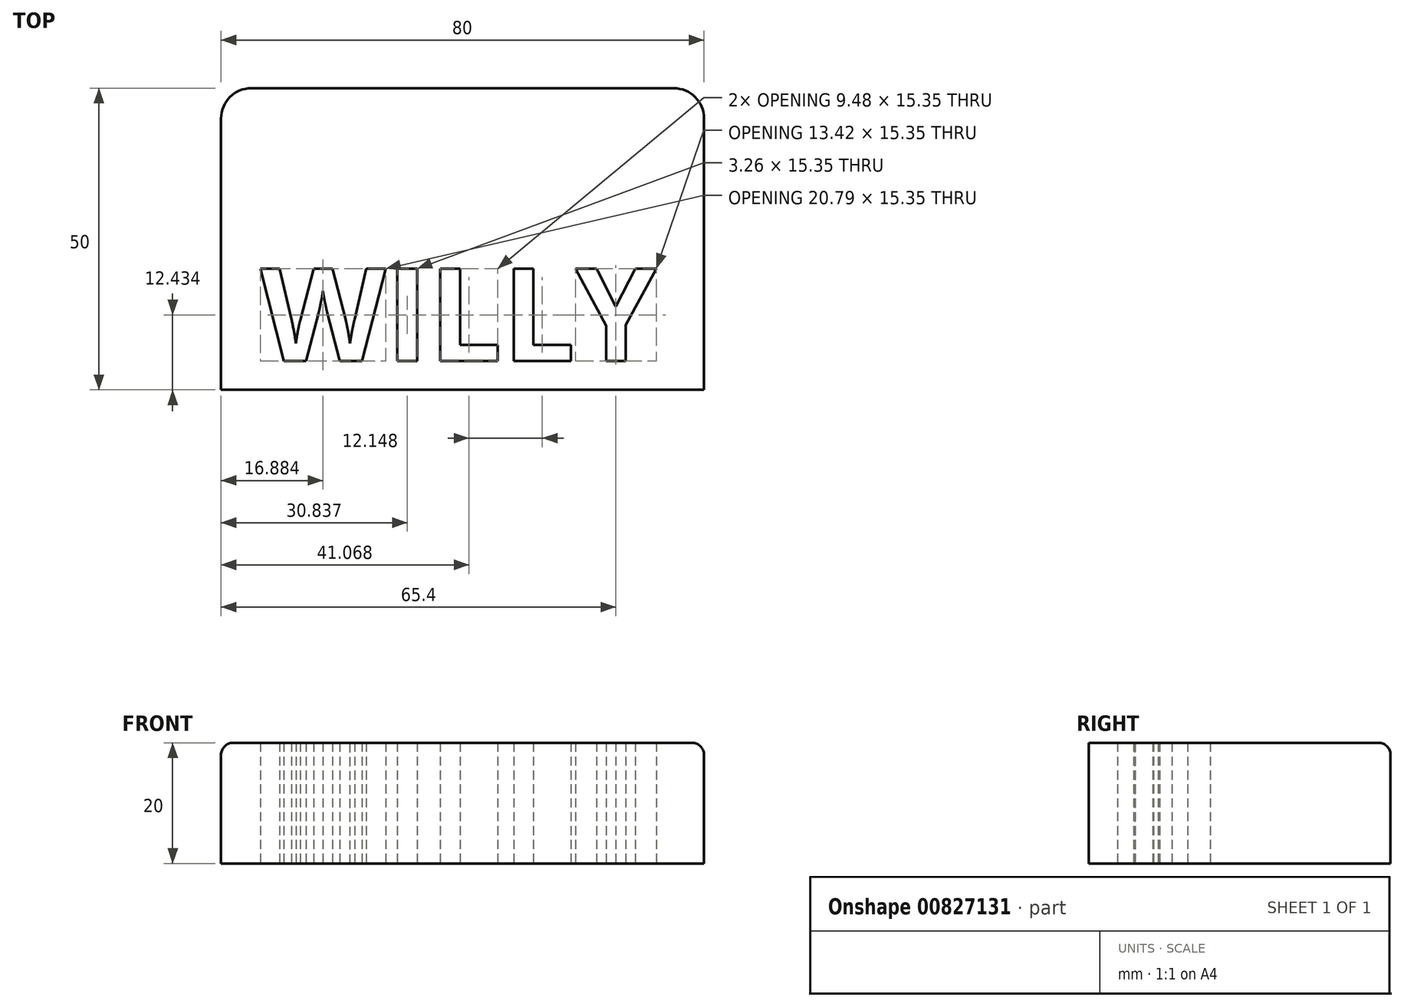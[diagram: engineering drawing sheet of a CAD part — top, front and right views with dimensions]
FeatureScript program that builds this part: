
annotation { "Feature Type Name" : "Feature", "Feature Type Description" : "" }
export const myFeature = defineFeature(function(context is Context, id is Id, definition is map)
    precondition{}
    {
        {
            var Q0;
            Q0=qCreatedBy(makeId("Top.planeOp"),FACE);
            var sketch = newSketch(context, id + "F0", { "sketchPlane" : qUnion([Q0])});
            skLineSegment(sketch, "E0.top", {"start": v(40, -25) * mm, "end": v(-40, -25) * mm});
            skLineSegment(sketch, "E0.left", {"start": v(40, 20) * mm, "end": v(40, -25) * mm});
            skLineSegment(sketch, "E0.right", {"start": v(-40, 20) * mm, "end": v(-40, -25) * mm});
            skPoint(sketch, "E0.middle", {"position": v(0, 0) * mm});
            skArc(sketch, "E1.filletArc", {"start": v(-35, 25) * mm, "mid": v(-38.54, 23.54) * mm, "end": v(-40, 20) * mm});
            skArc(sketch, "E2.filletArc", {"start": v(40, 20) * mm, "mid": v(38.54, 23.54) * mm, "end": v(35, 25) * mm});
            skPoint(sketch, "E3.middle", {"position": v(0, -12.5) * mm});
            skText(sketch, "E4", { "text": "WILLY", "fontName": "OpenSans-Bold.ttf"});
            skLineSegment(sketch, "E5", {"start": v(-35, 25) * mm, "end": v(35, 25) * mm});
            const initialGuessF0  = {"E4": [-0.03351, -0.02024, 1, 0, 0.01548]};
            skSetInitialGuess(sketch, initialGuessF0);
            skSolve(sketch);
        }
        {
            var Q0;
            Q0=makeQuery(id+"F0.imprint","IMPRINT",FACE,{"disambiguationData":[TD([[makeQuery(id+"F0.imprint","IMPRINT",EDGE,{"derivedFrom":sQuery(id+"F0.wireOp",EDGE,"E0.top")}),-1.0]])]});
            extrude(context, id + "F1", {"entities" : qUnion([Q0]), "depth" : 20 * mm, "offsetDistance" : 25 * mm});
        }
        {
            var Q0;
            Q0=makeQuery(id+"F1.opExtrude","CAP_EDGE",EDGE,{"disambiguationData":[OSD([sQuery(id+"F0.wireOp",EDGE,"E0.right")])],"isStart":false});
            fillet(context, id + "F2", {"entities" : qUnion([Q0]), "radius" : 2 * mm, "tangentPropagation" : true, "allowEdgeOverflow" : false});
        }
    });
